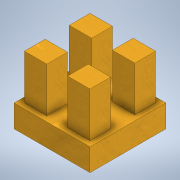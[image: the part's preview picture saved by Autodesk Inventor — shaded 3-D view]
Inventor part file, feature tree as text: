
AUTODESK INVENTOR PART (.ipt)
format: ipt  version: 2020 (Build 240168000, 168)  size: 144,384 bytes
history: native  units: mm
features: extrude x3, sketch x3
ambient origin geometry x8: Origin, YZ Plane, XZ Plane, XY Plane, X Axis, Y Axis, Z Axis, Center Point
bodies: Solid1 (feature_tree)
feature tree (6):
  extrude  "Extrusion1"  Depth=11.0mm
  extrude  "Extrusion2"  Depth=9.0mm
  extrude  "Extrusion3"  Depth=1.0mm TaperAngle=0.0deg
  sketch  "Sketch1"  dims[d0=11.0mm d1=11.0mm]
  sketch  "Sketch2"  dims[d2=3.25mm d3=0.0mm d4=9.0mm]
  sketch  "Sketch3"  dims[d5=9.0mm d6=1.0mm d7=0.0mm d8=3.25mm d9=3.0mm d10=0.75mm d11=0.75mm d12=20.0mm d14=6.5mm d15=20.0mm d17=6.25mm d20=6.5mm d21=0.0mm]
